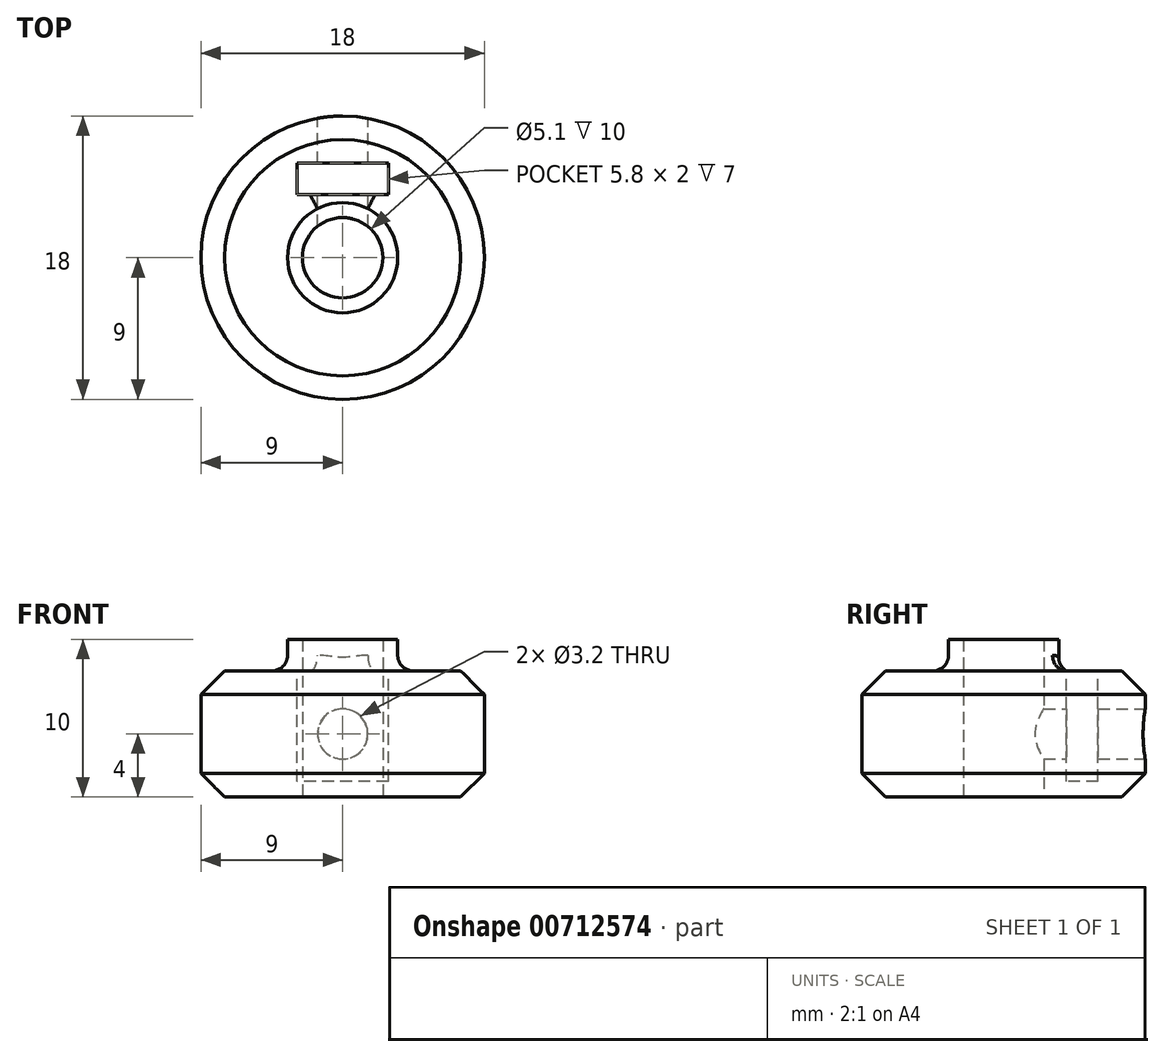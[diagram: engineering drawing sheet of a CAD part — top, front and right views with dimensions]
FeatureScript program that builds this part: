
annotation { "Feature Type Name" : "Feature", "Feature Type Description" : "" }
export const myFeature = defineFeature(function(context is Context, id is Id, definition is map)
    precondition{}
    {
        {
            var Q0;
            Q0=qCreatedBy(makeId("Front.planeOp"),FACE);
            var sketch = newSketch(context, id + "F0", { "sketchPlane" : qUnion([Q0])});
            skLineSegment(sketch, "E0", {"start": v(0, 0) * mm, "end": v(0, 20) * mm, "construction": true});
            skLineSegment(sketch, "E1", {"start": v(2.55, 0) * mm, "end": v(9, 0) * mm});
            skLineSegment(sketch, "E2", {"start": v(9, 0) * mm, "end": v(9, 8) * mm});
            skLineSegment(sketch, "E3", {"start": v(9, 8) * mm, "end": v(3.5, 8) * mm});
            skLineSegment(sketch, "E4", {"start": v(3.5, 8) * mm, "end": v(3.5, 10) * mm});
            skLineSegment(sketch, "E5", {"start": v(3.5, 10) * mm, "end": v(2.55, 10) * mm});
            skLineSegment(sketch, "E6", {"start": v(2.55, 10) * mm, "end": v(2.55, 0) * mm});
            skSolve(sketch);
        }
        {
            var Q0;
            Q0 = qSketchRegion(id + "F0", true);
            var Q1;
            Q1=sQuery(id+"F0.wireOp",EDGE,"E0");
            revolve(context, id + "F1", {"surfaceOperationType" : NewSurfaceOperationType.NEW, "entities" : qUnion([Q0]), "axis" : qUnion([Q1]), "revolveType" : RevolveType.FULL});
        }
        {
            var Q0;
            Q0=makeQuery(id+"F1.opRevolve","SWEPT_FACE",FACE,{"disambiguationData":[OSD([sQuery(id+"F0.wireOp",EDGE,"E3")])]});
            var sketch = newSketch(context, id + "F2", { "sketchPlane" : qUnion([Q0])});
            skLineSegment(sketch, "E7", {"start": v(0, 0) * mm, "end": v(0, 16.53) * mm, "construction": true});
            skLineSegment(sketch, "E8.bottom", {"start": v(2.9, 6) * mm, "end": v(-2.9, 6) * mm});
            skLineSegment(sketch, "E8.top", {"start": v(2.9, 4) * mm, "end": v(-2.9, 4) * mm});
            skLineSegment(sketch, "E8.left", {"start": v(2.9, 6) * mm, "end": v(2.9, 4) * mm});
            skLineSegment(sketch, "E8.right", {"start": v(-2.9, 6) * mm, "end": v(-2.9, 4) * mm});
            skPoint(sketch, "E8.middle", {"position": v(0, 5) * mm});
            skSolve(sketch);
        }
        {
            var Q0;
            Q0=makeQuery(id+"F2.imprint","IMPRINT",FACE,{"disambiguationData":[TD([[makeQuery(id+"F2.imprint","IMPRINT",EDGE,{"derivedFrom":sQuery(id+"F2.wireOp",EDGE,"E8.bottom")}),1.0]])]});
            extrude(context, id + "F3", {"entities" : qUnion([Q0]), "operationType" : NewBodyOperationType.REMOVE, "oppositeDirection" : true, "depth" : 7 * mm, "offsetDistance" : 25 * mm});
        }
        {
            var Q0;
            Q0=qCreatedBy(makeId("Front.planeOp"),FACE);
            cPlane(context, id + "F4", {"entities" : qUnion([Q0]), "cplaneType" : CPlaneType.OFFSET, "offset" : 10 * mm, "oppositeDirection" : true, "width" : 150 * mm, "height" : 150 * mm});
        }
        {
            var Q0;
            Q0=qCreatedBy(id+"F4.planeOp",FACE);
            var sketch = newSketch(context, id + "F5", { "sketchPlane" : qUnion([Q0])});
            skLineSegment(sketch, "E9", {"start": v(0, 0) * mm, "end": v(0, 8) * mm, "construction": true});
            skCircle(sketch, "E10", {"center": v(0, 4) * mm, "radius": 1.6 * mm});
            skSolve(sketch);
        }
        {
            var Q0;
            Q0=makeQuery(id+"F5.imprint","IMPRINT",FACE,{"disambiguationData":[TD([[makeQuery(id+"F5.imprint","IMPRINT",EDGE,{"derivedFrom":sQuery(id+"F5.wireOp",EDGE,"E10")}),1.0]])]});
            var Q1;
            Q1=makeQuery(id+"F1.opRevolve","SWEPT_FACE",FACE,{"disambiguationData":[OSD([sQuery(id+"F0.wireOp",EDGE,"E6")])]});
            extrude(context, id + "F6", {"entities" : qUnion([Q0]), "operationType" : NewBodyOperationType.REMOVE, "endBound" : BoundingType.UP_TO_SURFACE, "depth" : 25 * mm, "endBoundEntityFace" : qUnion([Q1]), "offsetDistance" : 25 * mm});
        }
        {
            var Q0;
            Q0=makeQuery(id+"F1.opRevolve","SWEPT_EDGE",EDGE,{"disambiguationData":[OSD([sQuery(id+"F0.wireOp",EDGE,"E2"),sQuery(id+"F0.wireOp",EDGE,"E3")])]});
            var Q1;
            Q1=makeQuery(id+"F1.opRevolve","SWEPT_EDGE",EDGE,{"disambiguationData":[OSD([sQuery(id+"F0.wireOp",EDGE,"E1"),sQuery(id+"F0.wireOp",EDGE,"E2")])]});
            chamfer(context, id + "F7", {"entities" : qUnion([Q0, Q1]), "width" : 1.5 * mm, "tangentPropagation" : true});
        }
        {
            var Q0;
            Q0=makeQuery(id+"F1.opRevolve","SWEPT_EDGE",EDGE,{"disambiguationData":[OSD([sQuery(id+"F0.wireOp",EDGE,"E3"),sQuery(id+"F0.wireOp",EDGE,"E4")])]});
            fillet(context, id + "F8", {"entities" : qUnion([Q0]), "radius" : 1 * mm, "tangentPropagation" : true, "allowEdgeOverflow" : false});
        }
    });
